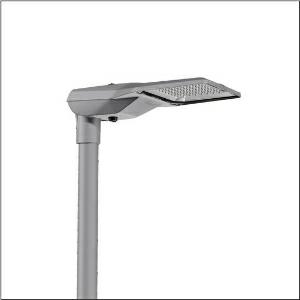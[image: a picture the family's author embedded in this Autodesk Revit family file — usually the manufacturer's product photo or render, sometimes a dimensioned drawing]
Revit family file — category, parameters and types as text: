
# Revit family: streetlight_sl_21_iq_midi___st1_0a_5xe3d51y08mb_fe0f
name_source: partatom
category: Lighting Fixtures
units: mm (PartAtom-declared; Revit-internal decimal feet)

## family parameters
Cut with Voids When Loaded = No
Host = Face
Light Source = No
Part Type = Normal
Room Calculation Point = No
Round Connector Dimension = Use Diameter
Shared = No

## types (1)
- --- (1 x LED, 16100 lm, 129.3 W, 3000K)
    Apparent Load = 129 VA
    CIE Flux Codes = 37 72 97 100 100
    Color Rendering = 80
    Color Temperature = 3000K
    Default Elevation = 1800 mm
    Description = Streetlight SL 21 iQ midi, mast luminaire, primary light control with lens, of PMMA, primary optical cover: cover, of toughened safety glass, transparent, light distribution: ST1.0a, light emission: direct distribution, primary light characteristic: asymmetric, installation type: post-top, side-entry, LED, High Power LED, rated luminous flux: 16.100lm, luminous efficacy: 125lm/W, light colour: 830, colour temperature: 3000K, control gear: iQ-Street Remote, D4i with power reduction, control: pre-setting: logarithmic dimming characteristic, Street-Remote, Auto-Match, Temp-Guard, Lumen-Switch, Night-Set, Smart-Wire, Light-Fading, Desk-Remote (wireless, voltage-free reading and setting of iQ features in the workshop via application-optimized NFC function/RFID function), optimised constant luminous flux control (CLO 2.0), mains connection: 230..240V, AC, 50/60Hz, start of lifetime: 129W, end of service life: 142W, reduction: 56W, luminaire housing, of diecast aluminium, powder-coated, SITECO metallic grey (DB 702S), corrosivity category C5 high according to DIN EN ISO 12944, please order mast flange separately, inclination adjustable: 0°, 5°, 10°, 15°, sealing non-destructively replaceable, multi-level sealing system, length: 644mm, width: 335mm, height: 110mm, mast flange for spigot size: 42mm (side-entry): 5XC10008XM4, 60/48mm (side-entry/post-top): 5XC10108XM2, 76/60mm (side-entry/post-top): 5XC10108XM1, mounting height: 4..8m, Smart Interface below and above, protection rating (complete): IP66, insulation class (complete): insulation class II (safety insulation), certification: CE, ENEC, ENEC+, VDE, impact resistance: IK10, permissible operating ambient temperature for outdoor applications: -40..+50°C, standard-compliant lighting for roads and squares, packaging unit: 1 piece

Light Distribution: ST1.0a
    Height = 111 mm
    Lamp = 1 x LED
    Lamp Light Flux = 16100 lm
    Lamp Power = 129.3 W
    Lamp count = 1
    Length = 644 mm
    Luminous efficacy = 125 lm/W
    Manufacturer = Siteco
    ModVariant = No
    Model = 5XE3D51Y08MB
    Number of Poles = 1
    OnlyDefault = Yes
    Power Factor = 1
    Product Name = Streetlight SL 21 iQ midi | ST1.0a
    Product group = mast luminaire | pylon top
    ProductGroupID = 6100
    Protection Class = Protection class II
    Protection Degree = IP 66
    RLX_Detail_Level = 1
    RLX_Emergency_Light_Flux = 0 lm
    RLX_Emergency_Type = 0
    RLX_Emergency_Type_DB = No
    RlxData = <blob elided: 91217 chars, md5=f0bb8d4e>
    Socket = socket
    Standby Power = 0 W
    System Light Flux = 16100 lm
    System Power = 129 W
    Type Comments = factory setting: luminous flux: 100 % | dim-lin: 254 | 672 mA
    Type Image = l_1004304.jpg
    URL = http://relux.com
    VarID = @adj_114615
    Voltage = 0 V
    Weight = 0.00 kg
    Width = 336 mm

## geometry (parser evidence)
native form markers: Blend x4, Sweep x11
no freeform markers — native parametric forms only
